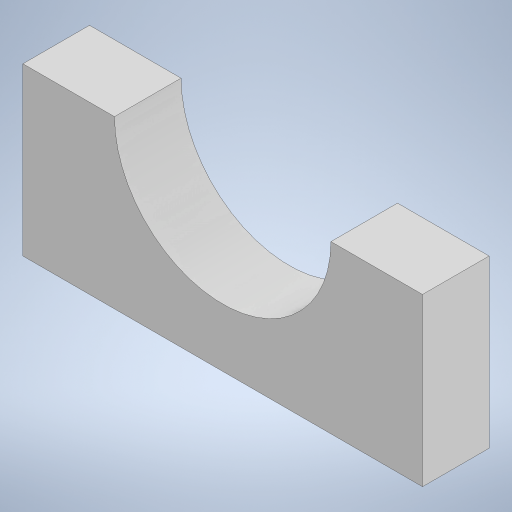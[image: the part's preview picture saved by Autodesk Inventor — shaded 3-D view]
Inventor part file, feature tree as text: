
AUTODESK INVENTOR PART (.ipt)
format: ipt  version: 2023 (Build 270158000, 158)  size: 208,384 bytes
history: native  units: in
note: dims shown in document units (in); Inventor stores cm internally (conversion verified against a paired STEP export)
features: extrude x1, sketch x1
ambient origin geometry x8: Origin, YZ Plane, XZ Plane, XY Plane, X Axis, Y Axis, Z Axis, Center Point
bodies: Body1 (feature_tree)
feature tree (2):
  extrude  "Extrusion4"  Depth=1.25in
  sketch  "Sketch1"  dims[d21=1.25in d22=1.25in d23=0.5in d24=0.0in]
